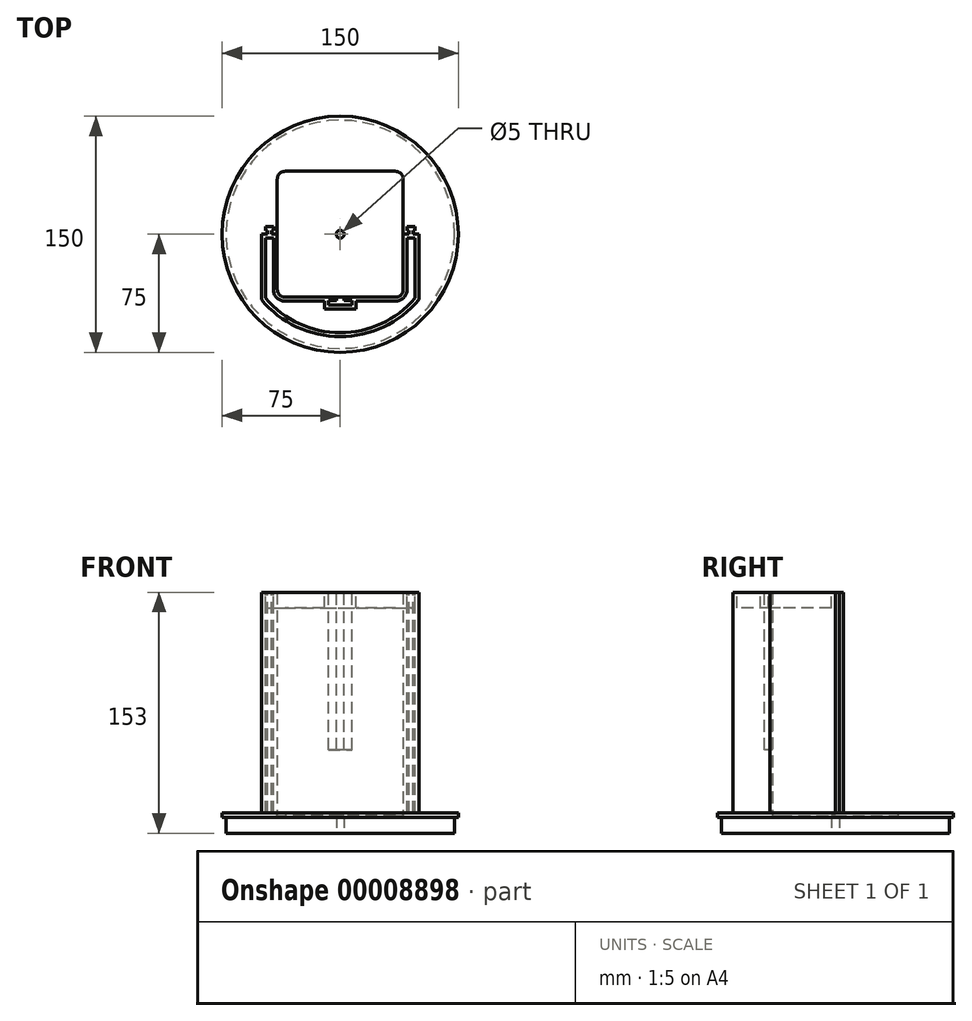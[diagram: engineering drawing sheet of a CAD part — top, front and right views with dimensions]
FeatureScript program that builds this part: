
annotation { "Feature Type Name" : "Feature", "Feature Type Description" : "" }
export const myFeature = defineFeature(function(context is Context, id is Id, definition is map)
    precondition{}
    {
        {
            var Q0;
            Q0=qCreatedBy(makeId("Top.planeOp"),FACE);
            var sketch = newSketch(context, id + "F0", { "sketchPlane" : qUnion([Q0])});
            skCircle(sketch, "E0", {"center": v(0, 0) * mm, "radius": 75 * mm});
            skSolve(sketch);
        }
        {
            var Q0;
            Q0=makeQuery(id+"F0.imprint","IMPRINT",FACE,{"disambiguationData":[TD([[makeQuery(id+"F0.imprint","IMPRINT",EDGE,{"derivedFrom":sQuery(id+"F0.wireOp",EDGE,"E0")}),1.0]])]});
            extrude(context, id + "F1", {"entities" : qUnion([Q0]), "oppositeDirection" : true, "depth" : 13 * mm});
        }
        {
            var Q0;
            Q0=makeQuery(id+"F1.opExtrude","CAP_FACE",FACE,{"disambiguationData":[OSD([sQuery(id+"F0.wireOp",EDGE,"E0")])],"isStart":true});
            var sketch = newSketch(context, id + "F2", { "sketchPlane" : qUnion([Q0])});
            skSolve(sketch);
        }
        {
            var Q0;
            Q0=makeQuery(id+"F2.imprint","IMPRINT",FACE,{"disambiguationData":[TD([[makeQuery(id+"F2.imprint","IMPRINT",EDGE,{"derivedFrom":makeQuery(id+"F1.opExtrude","CAP_EDGE",EDGE,{"disambiguationData":[OSD([sQuery(id+"F0.wireOp",EDGE,"E0")])],"isStart":true})}),1.0]])]});
            var sketch = newSketch(context, id + "F3", { "sketchPlane" : qUnion([Q0])});
            skLineSegment(sketch, "E1", {"start": v(55, 0) * mm, "end": v(-55, 0) * mm});
            skLineSegment(sketch, "E2", {"start": v(0, 0) * mm, "end": v(0, -35) * mm});
            skLineSegment(sketch, "E3.0.MirrorCS", {"start": v(0, 0) * mm, "end": v(0, 35) * mm});
            skCircle(sketch, "E4.0", {"center": v(0, 0) * mm, "radius": 65 * mm});
            skPoint(sketch, "E5.visualSharp", {"position": v(-45, -45) * mm});
            skPoint(sketch, "E6.visualSharp", {"position": v(45, -45) * mm});
            skPoint(sketch, "E7.visualSharp", {"position": v(-45, 45) * mm});
            skPoint(sketch, "E8.visualSharp", {"position": v(45, 45) * mm});
            skLineSegment(sketch, "E9.0", {"start": v(40, 0) * mm, "end": v(40, -35) * mm});
            skLineSegment(sketch, "E9.1", {"start": v(40, 0) * mm, "end": v(40, 35) * mm});
            skLineSegment(sketch, "E9.2", {"start": v(35, 40) * mm, "end": v(-35, 40) * mm});
            skLineSegment(sketch, "E9.3", {"start": v(-40, 0) * mm, "end": v(-40, 35) * mm});
            skLineSegment(sketch, "E9.4", {"start": v(-40, 0) * mm, "end": v(-40, -35) * mm});
            skLineSegment(sketch, "E9.5", {"start": v(35, -40) * mm, "end": v(-35, -40) * mm});
            skPoint(sketch, "E10.visualSharp", {"position": v(-40, 40) * mm});
            skArc(sketch, "E10.filletArc", {"start": v(-35, 40) * mm, "mid": v(-38.54, 38.54) * mm, "end": v(-40, 35) * mm});
            skPoint(sketch, "E11.visualSharp", {"position": v(40, 40) * mm});
            skArc(sketch, "E11.filletArc", {"start": v(40, 35) * mm, "mid": v(38.54, 38.54) * mm, "end": v(35, 40) * mm});
            skPoint(sketch, "E12.visualSharp", {"position": v(-40, -40) * mm});
            skArc(sketch, "E12.filletArc", {"start": v(-40, -35) * mm, "mid": v(-38.54, -38.54) * mm, "end": v(-35, -40) * mm});
            skPoint(sketch, "E13.visualSharp", {"position": v(40, -40) * mm});
            skArc(sketch, "E13.filletArc", {"start": v(35, -40) * mm, "mid": v(38.54, -38.54) * mm, "end": v(40, -35) * mm});
            skLineSegment(sketch, "E14.0", {"start": v(-50, 0) * mm, "end": v(-50, -41.53) * mm});
            skLineSegment(sketch, "E15.0", {"start": v(50, 0) * mm, "end": v(50, -41.53) * mm});
            skSolve(sketch);
        }
        {
            var Q0;
            {var subQ5=sQuery(id+"F3.wireOp",EDGE,"da40a887-6723-447c-b080-17973c0da07a.0");Q0=makeQuery(id+"F3.imprint","IMPRINT",FACE,{"disambiguationData":[TD([[makeQuery(id+"F3.imprint","IMPRINT",EDGE,{"derivedFrom":subQ5}),-1.0]])]});}
            var Q1;
            {var subQ3=sQuery(id+"F3.wireOp",EDGE,"E9.0");Q1=makeQuery(id+"F3.imprint","IMPRINT",FACE,{"disambiguationData":[TD([[makeQuery(id+"F3.imprint","IMPRINT",EDGE,{"derivedFrom":subQ3}),1.0]])]});}
            extrude(context, id + "F4", {"entities" : qUnion([Q0, Q1]), "operationType" : NewBodyOperationType.ADD, "depth" : 190 * mm});
        }
        {
            var Q0;
            Q0=makeQuery(id+"F4.opExtrude","CAP_FACE",FACE,{"disambiguationData":[OSD([sQuery(id+"F3.wireOp",EDGE,"E1"),sQuery(id+"F3.wireOp",EDGE,"288ae637-c1dc-4a47-9c3b-dad7fee5fc7e"),sQuery(id+"F3.wireOp",EDGE,"da40a887-6723-447c-b080-17973c0da07a.0"),sQuery(id+"F3.wireOp",EDGE,"7531d3ac-4d68-4d0d-a2ec-b46686c4fd53.0"),sQuery(id+"F3.wireOp",EDGE,"d73e7aac-ef0e-4b9c-b979-3aabb2721565.filletArc"),sQuery(id+"F3.wireOp",EDGE,"92710a06-4b23-40dd-95dd-d93b9efe6d8a.filletArc"),sQuery(id+"F3.wireOp",EDGE,"14ec5f45-ed82-458a-b0b5-23baf4c06ccb.0"),sQuery(id+"F3.wireOp",EDGE,"4be08ae0-8fd7-46e0-bcb6-398479c78f22.0"),sQuery(id+"F3.wireOp",EDGE,"30718d8a-f85b-44eb-b5a2-9b228f8a43ee.trimOffspring")])],"isStart":false});
            var sketch = newSketch(context, id + "F5", { "sketchPlane" : qUnion([Q0])});
            skLineSegment(sketch, "E16", {"start": v(-50, 0) * mm, "end": v(-50, 5) * mm});
            skLineSegment(sketch, "E17.0", {"start": v(-43.75, 0) * mm, "end": v(-43.75, 2.5) * mm});
            skLineSegment(sketch, "E18.0", {"start": v(-46.25, 0) * mm, "end": v(-46.25, 2.5) * mm});
            skLineSegment(sketch, "E19.0", {"start": v(-47.5, 2.5) * mm, "end": v(-47.5, 5) * mm});
            skLineSegment(sketch, "E20.0", {"start": v(-42.5, 2.5) * mm, "end": v(-42.5, 5) * mm});
            skLineSegment(sketch, "E21", {"start": v(-47.5, 5) * mm, "end": v(-42.5, 5) * mm});
            skLineSegment(sketch, "E22.0", {"start": v(-47.5, 2.5) * mm, "end": v(-46.25, 2.5) * mm});
            skLineSegment(sketch, "E23.trimOffspring", {"start": v(-43.75, 2.5) * mm, "end": v(-42.5, 2.5) * mm});
            skLineSegment(sketch, "E24", {"start": v(50, 0) * mm, "end": v(50, 5) * mm});
            skLineSegment(sketch, "E25.0", {"start": v(46.25, 0) * mm, "end": v(46.25, 2.5) * mm});
            skLineSegment(sketch, "E26.0", {"start": v(43.75, 0) * mm, "end": v(43.75, 2.5) * mm});
            skLineSegment(sketch, "E27.0", {"start": v(42.5, 2.5) * mm, "end": v(42.5, 5) * mm});
            skLineSegment(sketch, "E28.0", {"start": v(47.5, 2.5) * mm, "end": v(47.5, 5) * mm});
            skLineSegment(sketch, "E29", {"start": v(42.5, 5) * mm, "end": v(47.5, 5) * mm});
            skLineSegment(sketch, "E30.0", {"start": v(42.5, 2.5) * mm, "end": v(43.75, 2.5) * mm});
            skLineSegment(sketch, "E31.trimOffspring", {"start": v(46.25, 2.5) * mm, "end": v(47.5, 2.5) * mm});
            skSolve(sketch);
        }
        {
            var Q0;
            {var subQ3=sQuery(id+"F5.wireOp",EDGE,"E25.0");Q0=makeQuery(id+"F5.imprint","IMPRINT",FACE,{"disambiguationData":[TD([[makeQuery(id+"F5.imprint","IMPRINT",EDGE,{"derivedFrom":subQ3}),1.0]])]});}
            var Q1;
            {var subQ3=sQuery(id+"F5.wireOp",EDGE,"E17.0");Q1=makeQuery(id+"F5.imprint","IMPRINT",FACE,{"disambiguationData":[TD([[makeQuery(id+"F5.imprint","IMPRINT",EDGE,{"derivedFrom":subQ3}),1.0]])]});}
            extrude(context, id + "F6", {"entities" : qUnion([Q0, Q1]), "operationType" : NewBodyOperationType.ADD, "oppositeDirection" : true, "depth" : 190 * mm});
        }
        {
            var Q0;
            {var subQ0=sQuery(id+"F3.wireOp",EDGE,"E1");Q0=makeQuery(id+"F6.boolean.opBoolean","MERGE",FACE,{"derivedFrom":[makeQuery(id+"F4.opExtrude","CAP_FACE",FACE,{"disambiguationData":[OSD([subQ0,sQuery(id+"F3.wireOp",EDGE,"288ae637-c1dc-4a47-9c3b-dad7fee5fc7e"),sQuery(id+"F3.wireOp",EDGE,"da40a887-6723-447c-b080-17973c0da07a.0"),sQuery(id+"F3.wireOp",EDGE,"7531d3ac-4d68-4d0d-a2ec-b46686c4fd53.0"),sQuery(id+"F3.wireOp",EDGE,"d73e7aac-ef0e-4b9c-b979-3aabb2721565.filletArc"),sQuery(id+"F3.wireOp",EDGE,"92710a06-4b23-40dd-95dd-d93b9efe6d8a.filletArc"),sQuery(id+"F3.wireOp",EDGE,"14ec5f45-ed82-458a-b0b5-23baf4c06ccb.0"),sQuery(id+"F3.wireOp",EDGE,"4be08ae0-8fd7-46e0-bcb6-398479c78f22.0"),sQuery(id+"F3.wireOp",EDGE,"30718d8a-f85b-44eb-b5a2-9b228f8a43ee.trimOffspring")])],"isStart":false}),makeQuery(id+"F6.opExtrude","CAP_FACE",FACE,{"disambiguationData":[OSD([subQ0,sQuery(id+"F5.wireOp",EDGE,"fab437f5-0ac5-48c2-b438-e7b7dc68d477.0"),sQuery(id+"F5.wireOp",EDGE,"a4f9fca7-0a1a-4d7f-9eeb-7909bca0694d.0"),sQuery(id+"F5.wireOp",EDGE,"6cf46734-a90d-44c9-aa71-dbd65780f1c8.0"),sQuery(id+"F5.wireOp",EDGE,"ede3d52e-b7f4-4cb4-967b-7b2e52b34cc2.0"),sQuery(id+"F5.wireOp",EDGE,"0f755b23-2c73-44c1-a13d-9a2f4143ce92.0"),sQuery(id+"F5.wireOp",EDGE,"4c0356d8-34a5-41d7-a655-697f74d4b2fa.0"),sQuery(id+"F5.wireOp",EDGE,"731feb83-f851-40b8-9541-3379f316975e.0")])],"isStart":true}),makeQuery(id+"F6.opExtrude","CAP_FACE",FACE,{"disambiguationData":[OSD([subQ0,sQuery(id+"F5.wireOp",EDGE,"a5c5d2fd-144d-4496-b52d-f3ceec3b8255.0"),sQuery(id+"F5.wireOp",EDGE,"9dcfbb85-62a9-4b99-a6a1-c71cc165faac.0"),sQuery(id+"F5.wireOp",EDGE,"a5fbdf0b-598b-42ad-b754-e9e458963957.0"),sQuery(id+"F5.wireOp",EDGE,"5db33853-8a9c-45b7-8502-b66bb17395dc.0"),sQuery(id+"F5.wireOp",EDGE,"905a70d2-57c6-4490-96b9-09ff013b5af1.0"),sQuery(id+"F5.wireOp",EDGE,"e58c43ac-90d4-4cbf-8312-77f6fb28d84b.0"),sQuery(id+"F5.wireOp",EDGE,"143b045d-2d25-4ba5-9d8f-58c6dc93608e.0")])],"isStart":true})]});}
            var sketch = newSketch(context, id + "F7", { "sketchPlane" : qUnion([Q0])});
            skLineSegment(sketch, "E32.0", {"start": v(-33, -40) * mm, "end": v(33, -40) * mm});
            skLineSegment(sketch, "E33.0", {"start": v(7.5, -42) * mm, "end": v(2.5, -42) * mm});
            skLineSegment(sketch, "E34.0", {"start": v(-2.5, -42) * mm, "end": v(-7.5, -42) * mm});
            skLineSegment(sketch, "E35.0", {"start": v(-2.5, -45) * mm, "end": v(-7.5, -45) * mm});
            skLineSegment(sketch, "E36.0", {"start": v(7.5, -45) * mm, "end": v(2.5, -45) * mm});
            skLineSegment(sketch, "E37.0", {"start": v(-2.5, -45) * mm, "end": v(2.5, -45) * mm});
            skLineSegment(sketch, "E38", {"start": v(-2.5, -40) * mm, "end": v(-2.5, -42) * mm});
            skLineSegment(sketch, "E39", {"start": v(-7.5, -42) * mm, "end": v(-7.5, -45) * mm});
            skLineSegment(sketch, "E40", {"start": v(2.5, -40) * mm, "end": v(2.5, -42) * mm});
            skLineSegment(sketch, "E41", {"start": v(7.5, -42) * mm, "end": v(7.5, -45) * mm});
            skLineSegment(sketch, "E42", {"start": v(0, 0) * mm, "end": v(0, -51.24) * mm});
            skSolve(sketch);
        }
        {
            var Q0;
            Q0=makeQuery(id+"F7.imprint","IMPRINT",FACE,{"disambiguationData":[TD([[makeQuery(id+"F7.imprint","IMPRINT",EDGE,{"derivedFrom":sQuery(id+"F7.wireOp",EDGE,"E33.0")}),1.0]])]});
            var Q1;
            Q1=makeQuery(id+"F7.imprint","IMPRINT",FACE,{"disambiguationData":[TD([[makeQuery(id+"F7.imprint","IMPRINT",EDGE,{"derivedFrom":sQuery(id+"F7.wireOp",EDGE,"E34.0")}),1.0]])]});
            extrude(context, id + "F8", {"entities" : qUnion([Q0, Q1]), "operationType" : NewBodyOperationType.REMOVE, "oppositeDirection" : true, "depth" : 150 * mm});
        }
        {
            var Q0;
            {var subQ1=sQuery(id+"F3.wireOp",EDGE,"E9.1");Q0=makeQuery(id+"F3.imprint","IMPRINT",FACE,{"disambiguationData":[TD([[makeQuery(id+"F3.imprint","IMPRINT",EDGE,{"derivedFrom":subQ1}),1.0]])]});}
            var Q1;
            {var subQ1=sQuery(id+"F3.wireOp",EDGE,"E9.0");Q1=makeQuery(id+"F3.imprint","IMPRINT",FACE,{"disambiguationData":[TD([[makeQuery(id+"F3.imprint","IMPRINT",EDGE,{"derivedFrom":subQ1}),-1.0]])]});}
            extrude(context, id + "F9", {"entities" : qUnion([Q0, Q1]), "operationType" : NewBodyOperationType.REMOVE, "oppositeDirection" : true, "depth" : 2 * mm});
        }
        {
            var Q0;
            Q0=makeQuery(id+"F1.opExtrude","CAP_FACE",FACE,{"disambiguationData":[OSD([sQuery(id+"F0.wireOp",EDGE,"E0")])],"isStart":false});
            var sketch = newSketch(context, id + "F10", { "sketchPlane" : qUnion([Q0])});
            skCircle(sketch, "E43.0", {"center": v(0, 0) * mm, "radius": 72.5 * mm});
            skSolve(sketch);
        }
        {
            var Q0;
            Q0=makeQuery(id+"F10.imprint","IMPRINT",FACE,{"disambiguationData":[TD([[makeQuery(id+"F10.imprint","IMPRINT",EDGE,{"derivedFrom":sQuery(id+"F10.wireOp",EDGE,"E43.0")}),-1.0]])]});
            extrude(context, id + "F11", {"entities" : qUnion([Q0]), "operationType" : NewBodyOperationType.REMOVE, "oppositeDirection" : true, "depth" : 10 * mm});
        }
        {
            var Q0;
            Q0=makeQuery(id+"F1.opExtrude","CAP_FACE",FACE,{"disambiguationData":[OSD([sQuery(id+"F0.wireOp",EDGE,"E0")])],"isStart":false});
            var sketch = newSketch(context, id + "F12", { "sketchPlane" : qUnion([Q0])});
            skCircle(sketch, "E44", {"center": v(0, 0) * mm, "radius": 2.5 * mm});
            skSolve(sketch);
        }
        {
            var Q0;
            Q0=makeQuery(id+"F12.imprint","IMPRINT",FACE,{"disambiguationData":[TD([[makeQuery(id+"F12.imprint","IMPRINT",EDGE,{"derivedFrom":sQuery(id+"F12.wireOp",EDGE,"E44")}),1.0]])]});
            extrude(context, id + "F13", {"entities" : qUnion([Q0]), "operationType" : NewBodyOperationType.REMOVE, "oppositeDirection" : true, "depth" : 25 * mm});
        }
        {
            var Q0;
            {var subQ0=sQuery(id+"F3.wireOp",EDGE,"E1");Q0=makeQuery(id+"F6.boolean.opBoolean","MERGE",FACE,{"derivedFrom":[makeQuery(id+"F4.opExtrude","CAP_FACE",FACE,{"disambiguationData":[OSD([subQ0,sQuery(id+"F3.wireOp",EDGE,"E4.0"),sQuery(id+"F3.wireOp",EDGE,"E9.0"),sQuery(id+"F3.wireOp",EDGE,"E9.4"),sQuery(id+"F3.wireOp",EDGE,"E9.5"),sQuery(id+"F3.wireOp",EDGE,"E12.filletArc"),sQuery(id+"F3.wireOp",EDGE,"E13.filletArc"),sQuery(id+"F3.wireOp",EDGE,"E14.0"),sQuery(id+"F3.wireOp",EDGE,"E15.0")])],"isStart":false}),makeQuery(id+"F6.opExtrude","CAP_FACE",FACE,{"disambiguationData":[OSD([subQ0,sQuery(id+"F5.wireOp",EDGE,"E17.0"),sQuery(id+"F5.wireOp",EDGE,"E18.0"),sQuery(id+"F5.wireOp",EDGE,"E19.0"),sQuery(id+"F5.wireOp",EDGE,"E20.0"),sQuery(id+"F5.wireOp",EDGE,"E21"),sQuery(id+"F5.wireOp",EDGE,"E22.0"),sQuery(id+"F5.wireOp",EDGE,"E23.trimOffspring")])],"isStart":true}),makeQuery(id+"F6.opExtrude","CAP_FACE",FACE,{"disambiguationData":[OSD([subQ0,sQuery(id+"F5.wireOp",EDGE,"E25.0"),sQuery(id+"F5.wireOp",EDGE,"E26.0"),sQuery(id+"F5.wireOp",EDGE,"E27.0"),sQuery(id+"F5.wireOp",EDGE,"E28.0"),sQuery(id+"F5.wireOp",EDGE,"E29"),sQuery(id+"F5.wireOp",EDGE,"E30.0"),sQuery(id+"F5.wireOp",EDGE,"E31.trimOffspring")])],"isStart":true})]});}
            extrude(context, id + "F14", {"entities" : qUnion([Q0]), "operationType" : NewBodyOperationType.REMOVE, "oppositeDirection" : true, "depth" : 50 * mm});
        }
        {
            var Q0;
            Q0=makeQuery(id+"F14.boolean.opBoolean","COPY",FACE,{"derivedFrom":makeQuery(id+"F14.opExtrude","CAP_FACE",FACE,{"disambiguationData":[OSD([sQuery(id+"F3.wireOp",EDGE,"E1"),sQuery(id+"F3.wireOp",EDGE,"E4.0"),sQuery(id+"F3.wireOp",EDGE,"E9.0"),sQuery(id+"F3.wireOp",EDGE,"E9.4"),sQuery(id+"F3.wireOp",EDGE,"E9.5"),sQuery(id+"F3.wireOp",EDGE,"E12.filletArc"),sQuery(id+"F3.wireOp",EDGE,"E13.filletArc"),sQuery(id+"F3.wireOp",EDGE,"E14.0"),sQuery(id+"F3.wireOp",EDGE,"E15.0"),sQuery(id+"F5.wireOp",EDGE,"E17.0"),sQuery(id+"F5.wireOp",EDGE,"E18.0"),sQuery(id+"F5.wireOp",EDGE,"E19.0"),sQuery(id+"F5.wireOp",EDGE,"E20.0"),sQuery(id+"F5.wireOp",EDGE,"E21"),sQuery(id+"F5.wireOp",EDGE,"E22.0"),sQuery(id+"F5.wireOp",EDGE,"E23.trimOffspring"),sQuery(id+"F5.wireOp",EDGE,"E25.0"),sQuery(id+"F5.wireOp",EDGE,"E26.0"),sQuery(id+"F5.wireOp",EDGE,"E27.0"),sQuery(id+"F5.wireOp",EDGE,"E28.0"),sQuery(id+"F5.wireOp",EDGE,"E29"),sQuery(id+"F5.wireOp",EDGE,"E30.0"),sQuery(id+"F5.wireOp",EDGE,"E31.trimOffspring")])],"isStart":false})});
            var sketch = newSketch(context, id + "F15", { "sketchPlane" : qUnion([Q0])});
            skLineSegment(sketch, "E45", {"start": v(50, 0) * mm, "end": v(40, 0) * mm});
            skLineSegment(sketch, "E46", {"start": v(-50, 0) * mm, "end": v(-40, 0) * mm});
            skLineSegment(sketch, "E47.0", {"start": v(-47.5, -2.5) * mm, "end": v(-47.5, -40.62) * mm});
            skArc(sketch, "E47.1", {"start": v(-47.5, -40.62) * mm, "mid": v(0, -62.5) * mm, "end": v(47.5, -40.62) * mm});
            skLineSegment(sketch, "E47.2", {"start": v(47.5, -2.5) * mm, "end": v(47.5, -40.62) * mm});
            skLineSegment(sketch, "E47.3", {"start": v(47.5, -2.5) * mm, "end": v(42.5, -2.5) * mm});
            skLineSegment(sketch, "E47.4", {"start": v(42.5, -2.5) * mm, "end": v(42.5, -35) * mm});
            skLineSegment(sketch, "E47.5", {"start": v(-47.5, -2.5) * mm, "end": v(-42.5, -2.5) * mm});
            skArc(sketch, "E47.6", {"start": v(35, -42.5) * mm, "mid": v(40.3, -40.3) * mm, "end": v(42.5, -35) * mm});
            skLineSegment(sketch, "E47.7", {"start": v(35, -42.5) * mm, "end": v(10, -42.5) * mm});
            skLineSegment(sketch, "E47.9", {"start": v(-10, -42.5) * mm, "end": v(-35, -42.5) * mm});
            skArc(sketch, "E47.10", {"start": v(-42.5, -35) * mm, "mid": v(-40.3, -40.3) * mm, "end": v(-35, -42.5) * mm});
            skLineSegment(sketch, "E47.11", {"start": v(-42.5, -2.5) * mm, "end": v(-42.5, -35) * mm});
            skLineSegment(sketch, "E48", {"start": v(-2.5, -47.5) * mm, "end": v(-2.5, -49.1) * mm});
            skLineSegment(sketch, "E49", {"start": v(-10, -47.5) * mm, "end": v(10, -47.5) * mm});
            skLineSegment(sketch, "E50.0", {"start": v(-10, -42.5) * mm, "end": v(-10, -47.5) * mm});
            skLineSegment(sketch, "E51.0", {"start": v(10, -42.5) * mm, "end": v(10, -47.5) * mm});
            skSolve(sketch);
        }
        {
            var Q0;
            Q0=makeQuery(id+"F15.imprint","IMPRINT",FACE,{"disambiguationData":[TD([[makeQuery(id+"F15.imprint","IMPRINT",EDGE,{"derivedFrom":sQuery(id+"F15.wireOp",EDGE,"E47.0")}),1.0]])]});
            extrude(context, id + "F16", {"entities" : qUnion([Q0]), "operationType" : NewBodyOperationType.REMOVE, "oppositeDirection" : true, "depth" : 10 * mm});
        }
    });
